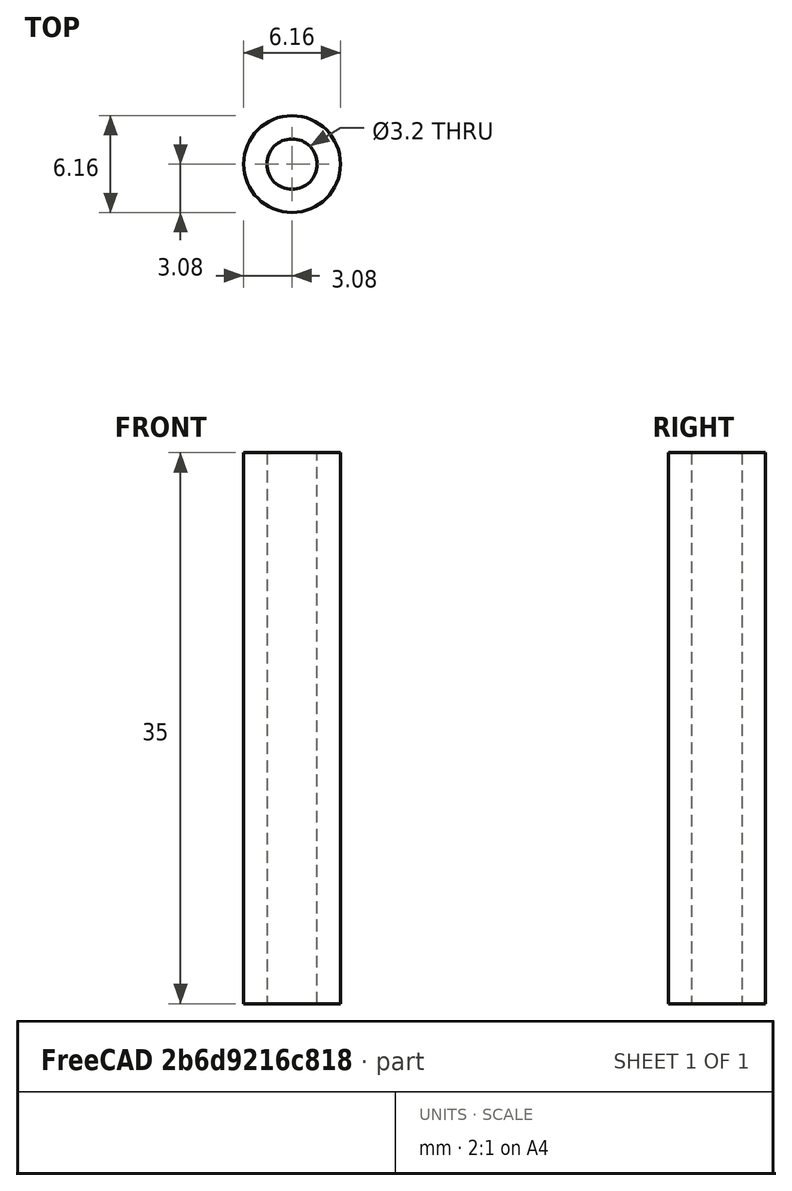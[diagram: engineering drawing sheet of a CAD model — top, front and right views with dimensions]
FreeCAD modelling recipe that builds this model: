
FCSTD DOCUMENT  (FreeCAD 0.20R29603 (Git))
Label: 6150-3200-35000
License: All rights reserved
LicenseURL: http://en.wikipedia.org/wiki/All_rights_reserved
objects: Sketcher::SketchObject×1, PartDesign::Pad×1, PartDesign::Body×1
note: 4 computed .brp shape members not serialized (recipe doc carries the construction recipe); baked Part::Feature solids carry a one-line shape summary decoded from their .brp

FEATURE [Sketcher::SketchObject] Sketch
  FullyConstrained = true
  MapMode = 5
  Support = -> [XY_Plane]
  sketch-geometry (2):
    g0: Circle CenterX=0 CenterY=0 CenterZ=0 NormalX=0 NormalY=0 NormalZ=1 AngleXU=0 Radius=3.075
    g1: Circle CenterX=0 CenterY=0 CenterZ=0 NormalX=0 NormalY=0 NormalZ=1 AngleXU=0 Radius=1.6
  constraints (4):
    c: Coincident(g0,g-1)
    c: Coincident(g1,g0)
    c: Radius(g1) = 1.6
    c: Radius(g0) = 3.075
FEATURE [PartDesign::Pad] Pad
  Direction = (0,0,1)
  Length = 35
  Length2 = 100
  Profile = -> Sketch
  ReferenceAxis = -> Sketch [N_Axis]
  Type = 0
FEATURE [PartDesign::Body] Body
  Group = -> [Sketch,Pad]
  Origin = -> Origin
  Tip = -> Pad
